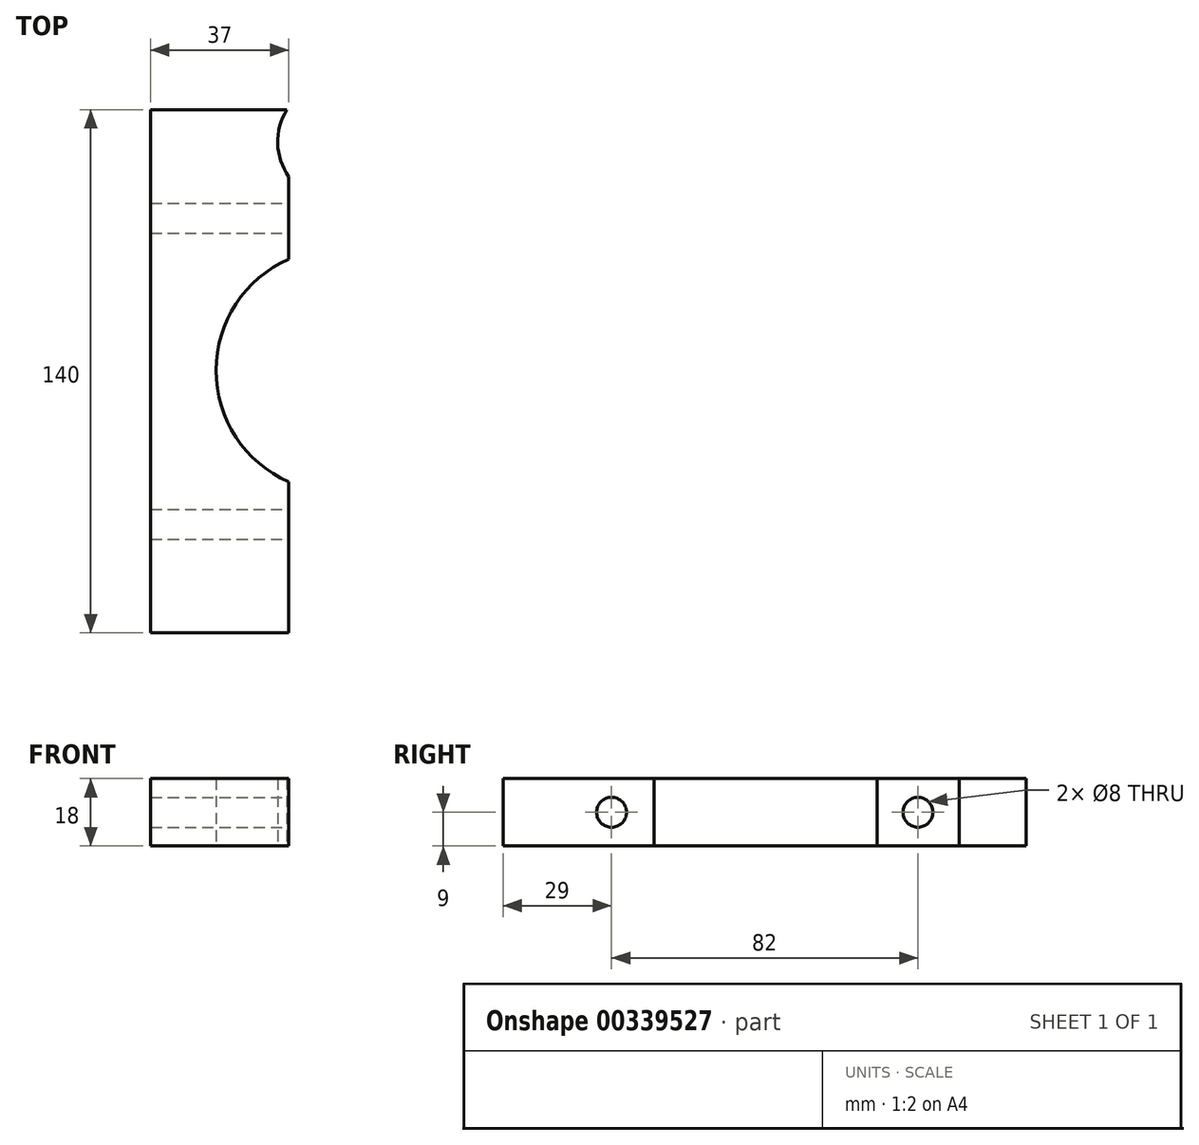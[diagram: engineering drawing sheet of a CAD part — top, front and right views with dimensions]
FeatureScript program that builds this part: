
annotation { "Feature Type Name" : "Feature", "Feature Type Description" : "" }
export const myFeature = defineFeature(function(context is Context, id is Id, definition is map)
    precondition{}
    {
        {
            var Q0;
            Q0=qCreatedBy(makeId("Top.planeOp"),FACE);
            var sketch = newSketch(context, id + "F0", { "sketchPlane" : qUnion([Q0])});
            skLineSegment(sketch, "E0.bottom", {"start": v(0, 0) * mm, "end": v(37, 0) * mm});
            skLineSegment(sketch, "E0.top", {"start": v(0, 140) * mm, "end": v(37, 140) * mm});
            skLineSegment(sketch, "E0.left", {"start": v(0, 0) * mm, "end": v(0, 140) * mm});
            skLineSegment(sketch, "E0.right", {"start": v(37, 0) * mm, "end": v(37, 140) * mm});
            skCircle(sketch, "E1", {"center": v(50, 70.21) * mm, "radius": 32.5 * mm});
            skLineSegment(sketch, "E2", {"start": v(0, 70) * mm, "end": v(50, 70.21) * mm, "construction": true});
            skCircle(sketch, "E3", {"center": v(50, 131.42) * mm, "radius": 16 * mm});
            skLineSegment(sketch, "E4", {"start": v(50, 131.42) * mm, "end": v(0, 131.42) * mm, "construction": true});
            skLineSegment(sketch, "E5", {"start": v(49.66, 115.42) * mm, "end": v(49.66, 102.71) * mm, "construction": true});
            skSolve(sketch);
        }
        {
            var Q0;
            Q0=makeQuery(id+"F0.imprint","IMPRINT",FACE,{"disambiguationData":[TD([[makeQuery(id+"F0.imprint","IMPRINT",EDGE,{"derivedFrom":sQuery(id+"F0.wireOp",EDGE,"E0.bottom")}),1.0]])]});
            extrude(context, id + "F1", {"entities" : qUnion([Q0]), "depth" : 18 * mm});
        }
        {
            var Q0;
            {var subQ0=sQuery(id+"F0.wireOp",EDGE,"E0.right");Q0=makeQuery(id+"F1.opExtrude","SWEPT_FACE",FACE,{"disambiguationData":[OSD([subQ0]),TDD([makeQuery(id+"F0.imprint","IMPRINT",EDGE,{"disambiguationData":[TD([[makeQuery(id+"F0.imprint","INTERSECT",VERTEX,{"derivedFrom":[sQuery(id+"F0.wireOp",EDGE,"E0.bottom"),subQ0]}),-1.0]])],"derivedFrom":subQ0})])]});}
            var sketch = newSketch(context, id + "F2", { "sketchPlane" : qUnion([Q0])});
            skLineSegment(sketch, "E6", {"start": v(0, 9) * mm, "end": v(140, 9) * mm, "construction": true});
            skPoint(sketch, "E6.endSnap0", {"position": v(40.43, 9) * mm});
            skCircle(sketch, "E7", {"center": v(29, 9) * mm, "radius": 4 * mm});
            skCircle(sketch, "E8", {"center": v(111, 9) * mm, "radius": 4 * mm});
            skSolve(sketch);
        }
        {
            var Q0;
            Q0=makeQuery(id+"F2.imprint","IMPRINT",FACE,{"disambiguationData":[TD([[makeQuery(id+"F2.imprint","IMPRINT",EDGE,{"derivedFrom":sQuery(id+"F2.wireOp",EDGE,"E8")}),1.0]])]});
            var Q1;
            Q1=makeQuery(id+"F2.imprint","IMPRINT",FACE,{"disambiguationData":[TD([[makeQuery(id+"F2.imprint","IMPRINT",EDGE,{"derivedFrom":sQuery(id+"F2.wireOp",EDGE,"E7")}),1.0]])]});
            extrude(context, id + "F3", {"entities" : qUnion([Q0, Q1]), "operationType" : NewBodyOperationType.REMOVE, "endBound" : BoundingType.THROUGH_ALL, "oppositeDirection" : true, "depth" : 25 * mm});
        }
    });
